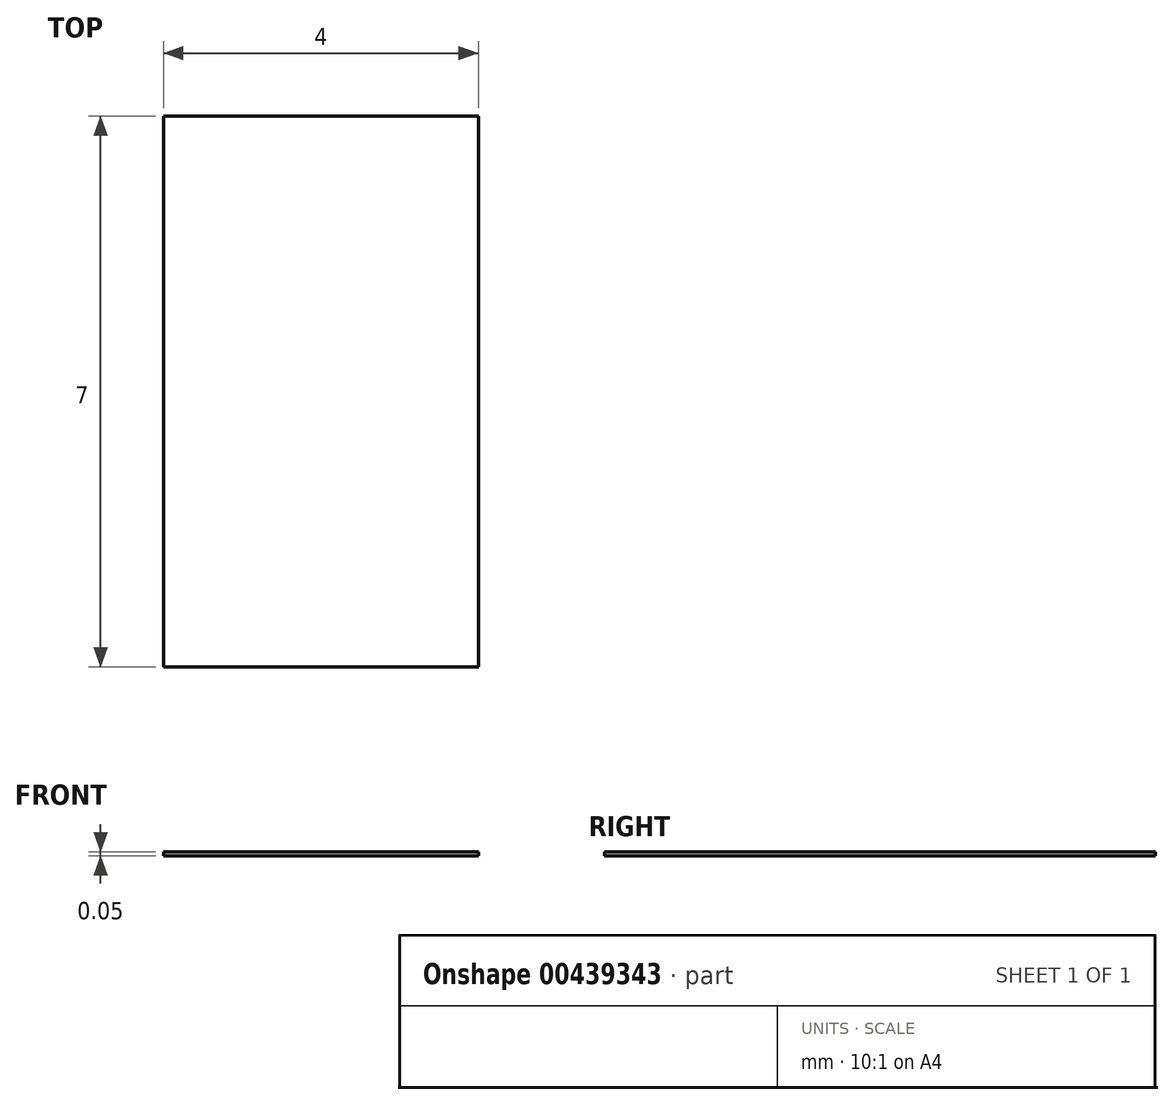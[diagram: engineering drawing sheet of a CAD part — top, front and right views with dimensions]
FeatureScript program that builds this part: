
annotation { "Feature Type Name" : "Feature", "Feature Type Description" : "" }
export const myFeature = defineFeature(function(context is Context, id is Id, definition is map)
    precondition{}
    {
        {
            var Q0;
            Q0=qCreatedBy(makeId("Top.planeOp"),FACE);
            var sketch = newSketch(context, id + "F0", { "sketchPlane" : qUnion([Q0])});
            skLineSegment(sketch, "E0.bottom", {"start": v(0, 0) * mm, "end": v(4, 0) * mm});
            skLineSegment(sketch, "E0.top", {"start": v(0, 7) * mm, "end": v(4, 7) * mm});
            skLineSegment(sketch, "E0.left", {"start": v(0, 0) * mm, "end": v(0, 7) * mm});
            skLineSegment(sketch, "E0.right", {"start": v(4, 0) * mm, "end": v(4, 7) * mm});
            skSolve(sketch);
        }
        {
            var Q0;
            Q0 = qSketchRegion(id + "F0", true);
            extrude(context, id + "F1", {"entities" : qUnion([Q0]), "depth" : 0.05 * mm});
        }
    });
